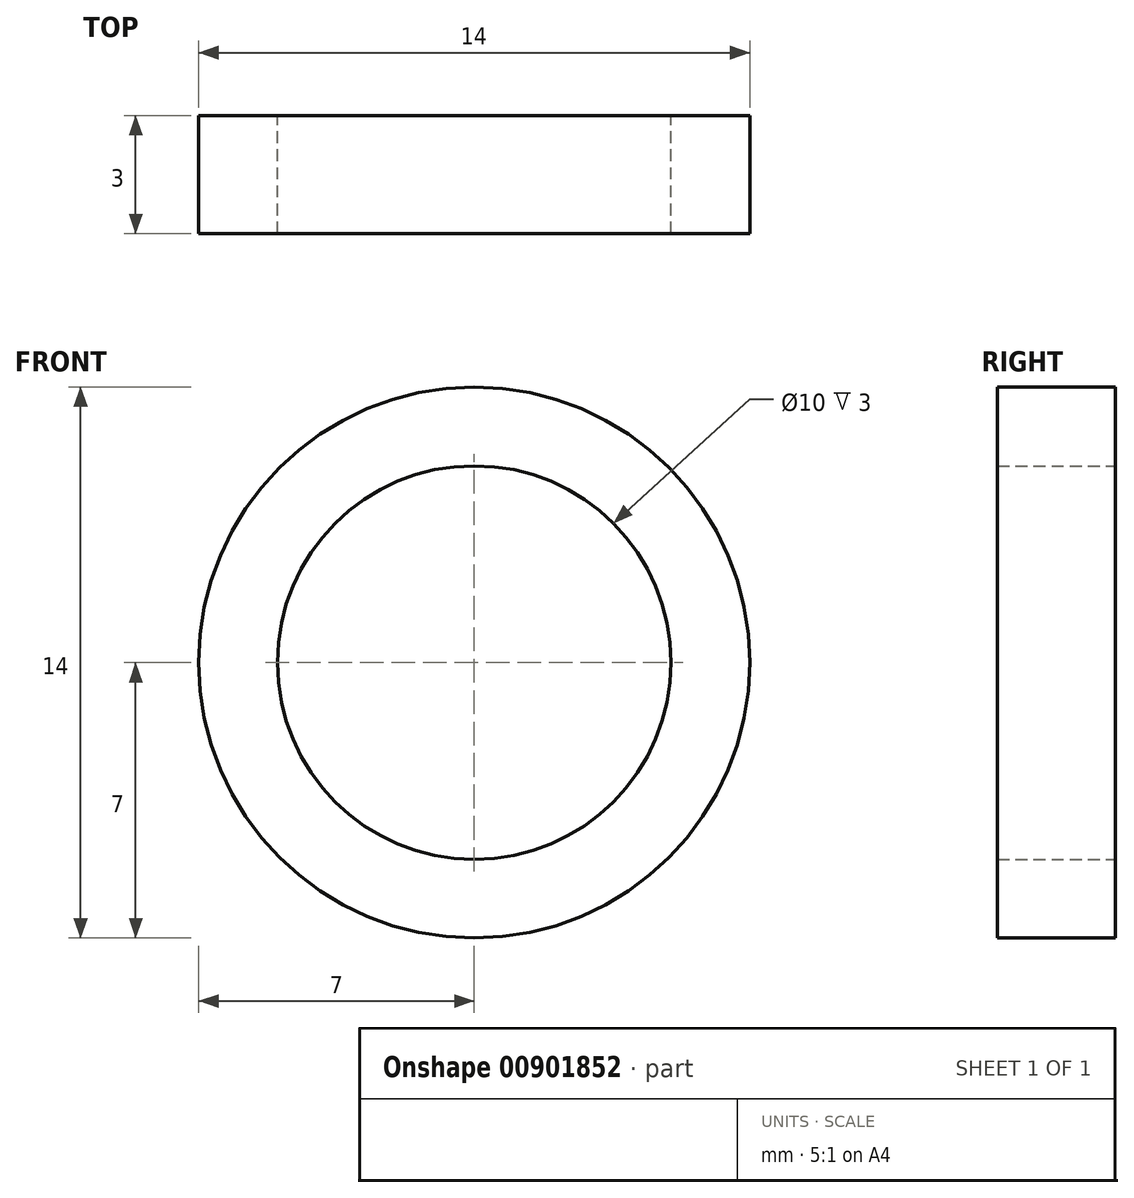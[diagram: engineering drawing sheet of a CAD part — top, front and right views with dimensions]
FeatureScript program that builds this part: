
annotation { "Feature Type Name" : "Feature", "Feature Type Description" : "" }
export const myFeature = defineFeature(function(context is Context, id is Id, definition is map)
    precondition{}
    {
        {
            var Q0;
            Q0=qCreatedBy(makeId("Front.planeOp"),FACE);
            var sketch = newSketch(context, id + "F0", { "sketchPlane" : qUnion([Q0])});
            skCircle(sketch, "E0", {"center": v(0, 0) * mm, "radius": 7 * mm});
            skCircle(sketch, "E1", {"center": v(0, 0) * mm, "radius": 5 * mm});
            skSolve(sketch);
        }
        {
            var Q0;
            Q0 = qSketchRegion(id + "F0", true);
            extrude(context, id + "F1", {"entities" : qUnion([Q0]), "depth" : 3 * mm, "offsetDistance" : 25 * mm});
        }
    });
